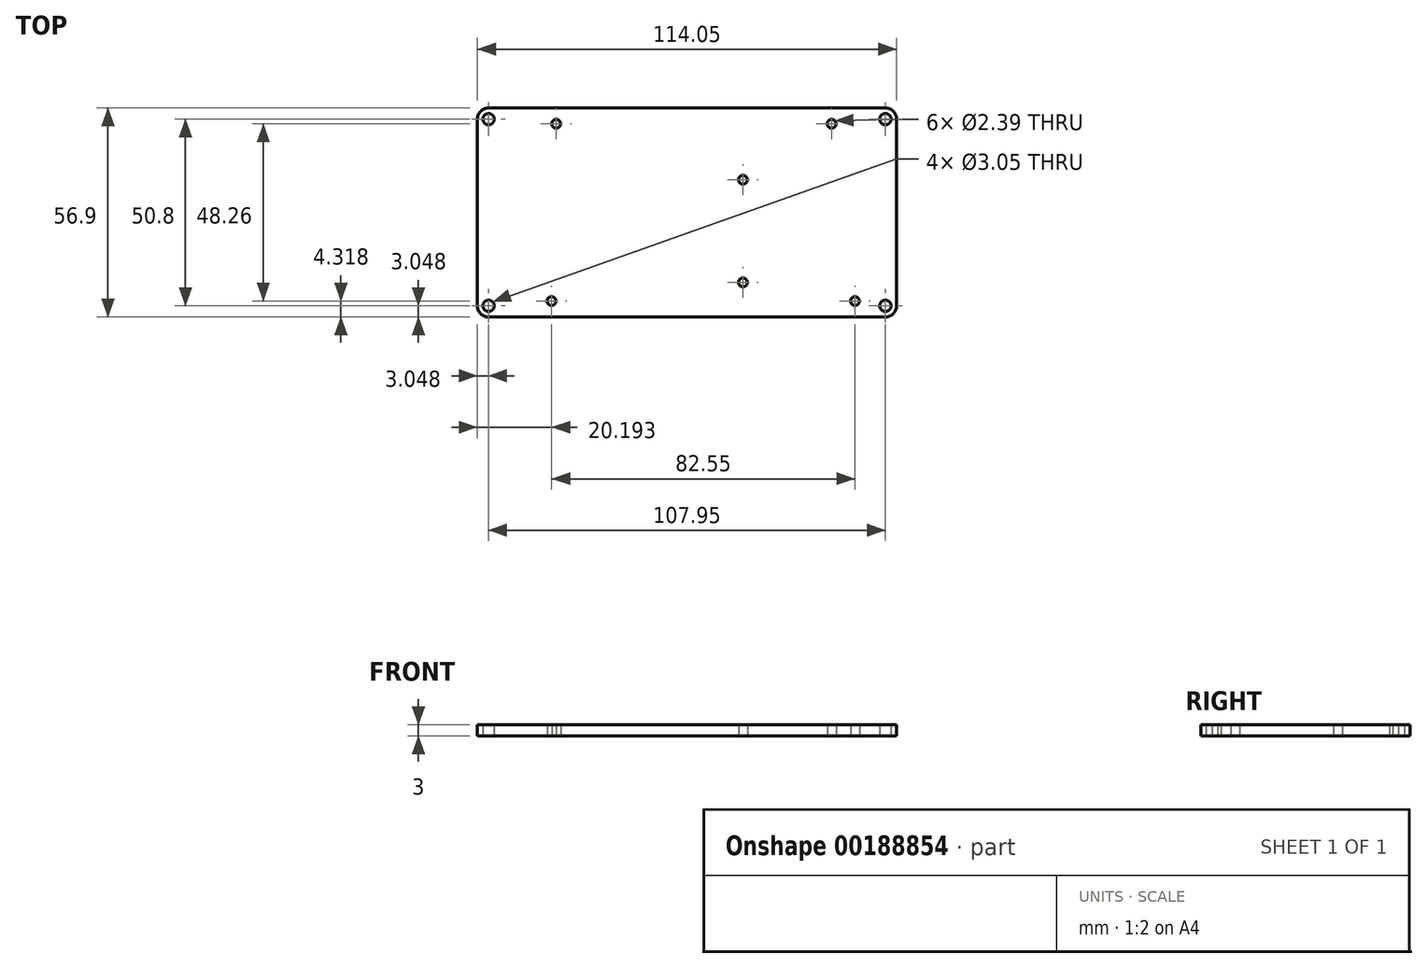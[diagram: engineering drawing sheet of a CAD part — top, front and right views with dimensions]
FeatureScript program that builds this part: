
annotation { "Feature Type Name" : "Feature", "Feature Type Description" : "" }
export const myFeature = defineFeature(function(context is Context, id is Id, definition is map)
    precondition{}
    {
        {
            var Q0;
            Q0=qCreatedBy(makeId("Top.planeOp"),FACE);
            var sketch = newSketch(context, id + "F0", { "sketchPlane" : qUnion([Q0])});
            skLineSegment(sketch, "E0.bottom", {"start": v(3.05, 0) * mm, "end": v(111, 0) * mm});
            skLineSegment(sketch, "E0.top", {"start": v(3.05, 56.9) * mm, "end": v(111, 56.9) * mm});
            skLineSegment(sketch, "E0.left", {"start": v(0, 3.05) * mm, "end": v(0, 53.85) * mm});
            skLineSegment(sketch, "E0.right", {"start": v(114.05, 3.05) * mm, "end": v(114.05, 53.85) * mm});
            skCircle(sketch, "E1", {"center": v(3.05, 3.05) * mm, "radius": 1.52 * mm});
            skCircle(sketch, "E2", {"center": v(3.05, 53.85) * mm, "radius": 1.52 * mm});
            skCircle(sketch, "E3", {"center": v(111, 53.85) * mm, "radius": 1.52 * mm});
            skCircle(sketch, "E4", {"center": v(111, 3.05) * mm, "radius": 1.52 * mm});
            skCircle(sketch, "E5", {"center": v(21.46, 52.58) * mm, "radius": 1.2 * mm});
            skCircle(sketch, "E6", {"center": v(20.2, 4.32) * mm, "radius": 1.2 * mm});
            skCircle(sketch, "E7", {"center": v(72.26, 9.4) * mm, "radius": 1.2 * mm});
            skPoint(sketch, "E8.visualSharp", {"position": v(0, 56.9) * mm});
            skArc(sketch, "E8.filletArc", {"start": v(3.05, 56.9) * mm, "mid": v(0.9, 56) * mm, "end": v(0, 53.85) * mm});
            skPoint(sketch, "E9.visualSharp", {"position": v(114.05, 56.9) * mm});
            skArc(sketch, "E9.filletArc", {"start": v(114.05, 53.85) * mm, "mid": v(113.15, 56) * mm, "end": v(111, 56.9) * mm});
            skPoint(sketch, "E10.visualSharp", {"position": v(114.05, 0) * mm});
            skArc(sketch, "E10.filletArc", {"start": v(111, 0) * mm, "mid": v(113.15, 0.9) * mm, "end": v(114.05, 3.05) * mm});
            skPoint(sketch, "E11.visualSharp", {"position": v(0, 0) * mm});
            skArc(sketch, "E11.filletArc", {"start": v(0, 3.05) * mm, "mid": v(0.9, 0.9) * mm, "end": v(3.05, 0) * mm});
            skCircle(sketch, "E12", {"center": v(72.26, 37.34) * mm, "radius": 1.2 * mm});
            skCircle(sketch, "E13", {"center": v(96.4, 52.58) * mm, "radius": 1.2 * mm});
            skCircle(sketch, "E14", {"center": v(102.74, 4.32) * mm, "radius": 1.2 * mm});
            skSolve(sketch);
        }
        {
            var Q0;
            Q0=qSketchRegion(id+"F0",true);
            extrude(context, id + "F1", {"entities" : qUnion([Q0]), "depth" : 3 * mm});
        }
    });
